# Revit family: QF_ELECTROLUXPROFESSIONAL_391118_E9BSEHIPF0
name_source: partatom
category: Specialty Equipment
revit_build: Autodesk Revit 2018 (Build: 20190510_1515(x64)
units: mm (PartAtom-declared; Revit-internal decimal feet)

## family parameters
Always vertical = Yes
Cut with Voids When Loaded = No
Part Type = Normal
Room Calculation Point = No
Round Connector Dimension = Use Diameter
Shared = No
Work Plane-Based = No

## types (1)
- QF_ELECTROLUXPROFESSIONAL_391118_E9BSEHIPF0
    Apparent Power = 0 VA
    Cold Water Connection Height = 0 mm  [stored 0 ft]
    Cold Water Maximum Pressure = 0.00 psi
    Cold Water Minimum Pressure = 0.00 psi
    Cold Water Size = 1"
    Conn Conduit = Yes
    Depth = 930 mm
    Description = 900XP ELECTRIC CYLINDRICAL BOILING PAN 100LT - 400 V
    Direct Waste Size = 2"
    FL Amps = 0 A
    HP = 28.8 HP
    Height = 850 mm  [stored 2.78871 ft]
    Hot Water Connection Height = 0 mm  [stored 0 ft]
    Hot Water Consumption = 0 GPM
    Hot Water Maximum Pressure = 0.00 psi
    Hot Water Minimum Pressure = 0.00 psi
    Hot Water Size = 1"
    Indirect Waste Connection Height = 0 mm  [stored 0 ft]
    Indirect Waste Size = 1"
    Manufacturer = ELECTROLUX
    Max Overcurrent Protection = 0 A
    Min Ckt Ampacity = 0 A
    Model = 391118
    Phase = 3
    URL = www.electrolux.com
    URL Cutsheet = www.electrolux.com
    Volts = 400 V
    Watts = 0 W
    Weight in Pounds = 135
    Width = 800 mm  [stored 2.62467 ft]

note: [stored X ft] marks values corroborated as IEEE doubles in the binary element streams (Revit-internal decimal feet)

## geometry (parser evidence)
native form markers: Blend x9, Sweep x2
no freeform markers — native parametric forms only
